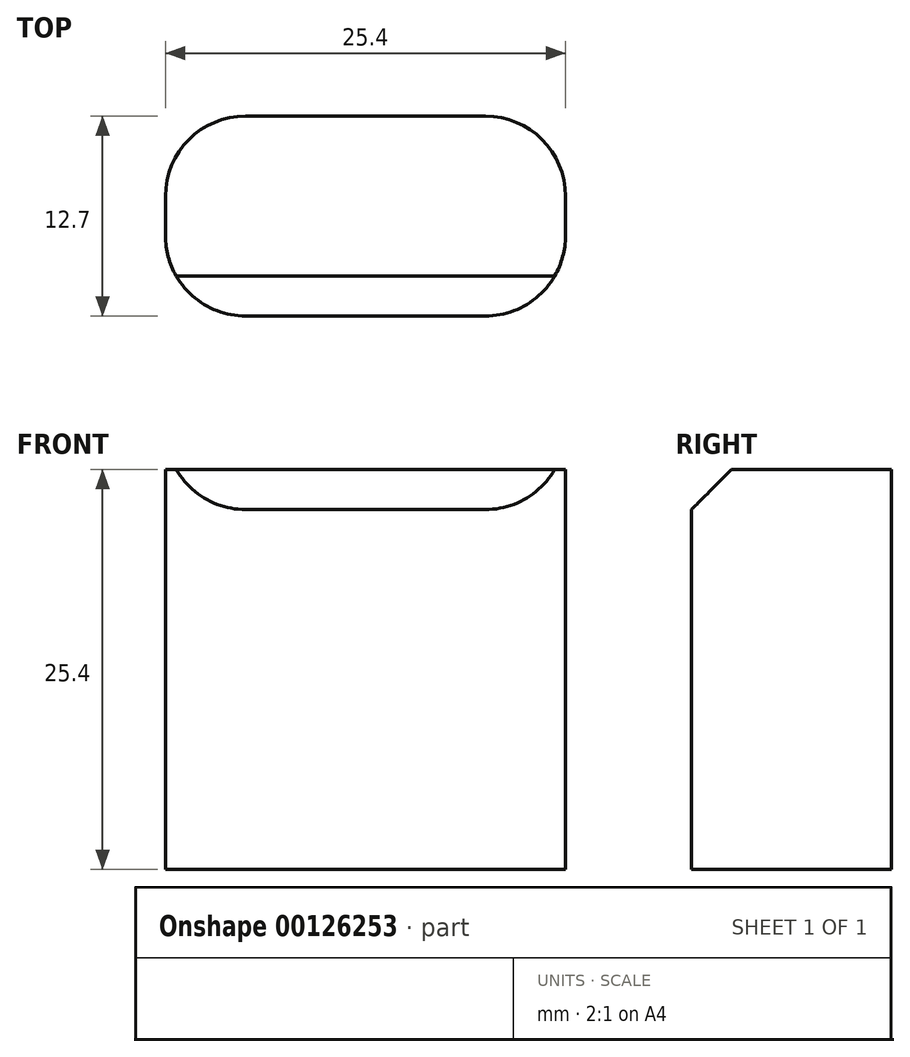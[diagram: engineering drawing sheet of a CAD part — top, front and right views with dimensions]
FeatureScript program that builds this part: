
annotation { "Feature Type Name" : "Feature", "Feature Type Description" : "" }
export const myFeature = defineFeature(function(context is Context, id is Id, definition is map)
    precondition{}
    {
        {
            var Q0;
            Q0=qCreatedBy(makeId("Top.planeOp"),FACE);
            var sketch = newSketch(context, id + "F0", { "sketchPlane" : qUnion([Q0])});
            skLineSegment(sketch, "E0.bottom", {"start": v(-20.07, 4.89) * mm, "end": v(5.33, 4.89) * mm});
            skLineSegment(sketch, "E0.top", {"start": v(-20.07, 17.59) * mm, "end": v(5.33, 17.59) * mm});
            skLineSegment(sketch, "E0.left", {"start": v(-20.07, 4.89) * mm, "end": v(-20.07, 17.59) * mm});
            skLineSegment(sketch, "E0.right", {"start": v(5.33, 4.89) * mm, "end": v(5.33, 17.59) * mm});
            skSolve(sketch);
        }
        {
            var Q0;
            Q0 = qSketchRegion(id + "F0", true);
            extrude(context, id + "F1", {"entities" : qUnion([Q0]), "depth" : 25.4 * mm});
        }
        {
            var Q0;
            Q0=makeQuery(id+"F1.opExtrude","SWEPT_EDGE",EDGE,{"disambiguationData":[OSD([sQuery(id+"F0.wireOp",EDGE,"E0.bottom"),sQuery(id+"F0.wireOp",EDGE,"E0.right")])]});
            var Q1;
            Q1=makeQuery(id+"F1.opExtrude","SWEPT_EDGE",EDGE,{"disambiguationData":[OSD([sQuery(id+"F0.wireOp",EDGE,"E0.top"),sQuery(id+"F0.wireOp",EDGE,"E0.right")])]});
            var Q2;
            Q2=makeQuery(id+"F1.opExtrude","SWEPT_EDGE",EDGE,{"disambiguationData":[OSD([sQuery(id+"F0.wireOp",EDGE,"E0.top"),sQuery(id+"F0.wireOp",EDGE,"E0.left")])]});
            var Q3;
            Q3=makeQuery(id+"F1.opExtrude","SWEPT_EDGE",EDGE,{"disambiguationData":[OSD([sQuery(id+"F0.wireOp",EDGE,"E0.bottom"),sQuery(id+"F0.wireOp",EDGE,"E0.left")])]});
            fillet(context, id + "F2", {"entities" : qUnion([Q0, Q1, Q2, Q3]), "radius" : 5.08 * mm, "tangentPropagation" : true, "allowEdgeOverflow" : false});
        }
        {
            var Q0;
            Q0=makeQuery(id+"F1.opExtrude","CAP_EDGE",EDGE,{"disambiguationData":[OSD([sQuery(id+"F0.wireOp",EDGE,"E0.bottom")])],"isStart":false});
            chamfer(context, id + "F3", {"entities" : qUnion([Q0]), "width" : 2.54 * mm});
        }
    });
